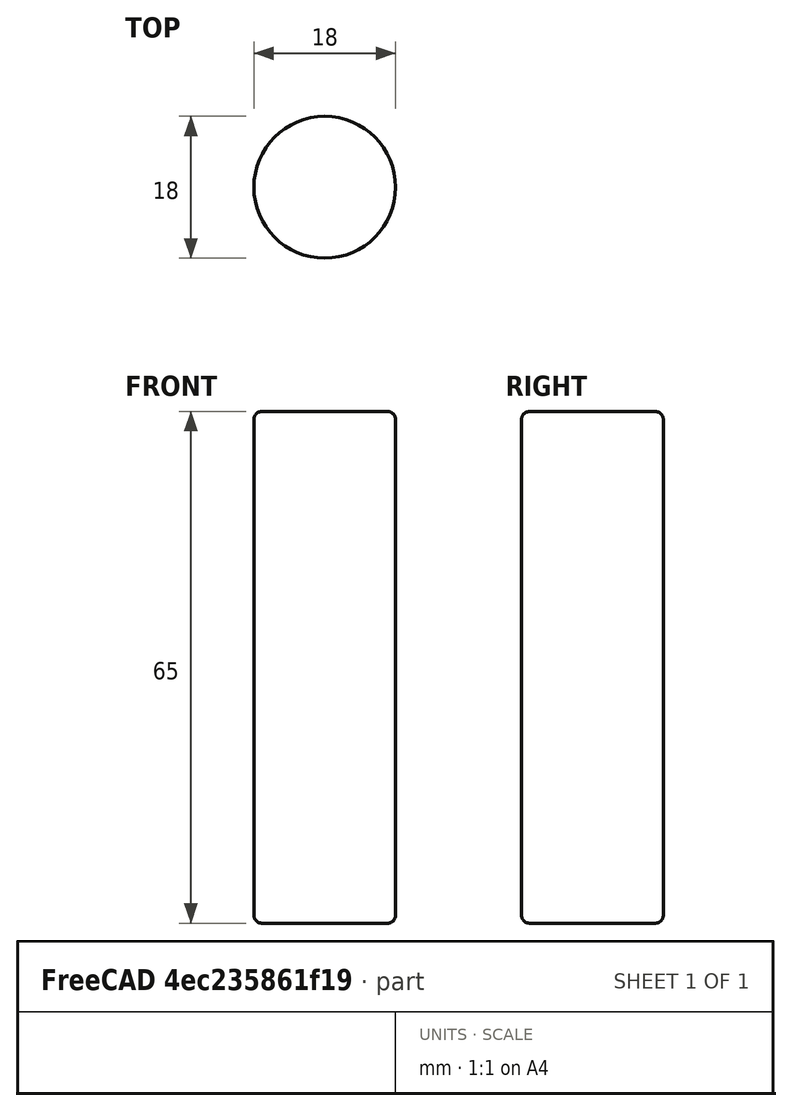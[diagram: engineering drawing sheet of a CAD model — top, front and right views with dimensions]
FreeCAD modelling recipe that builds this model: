
FCSTD DOCUMENT  (FreeCAD 0.20R29603 (Git))
Label: Battery
License: All rights reserved
LicenseURL: http://en.wikipedia.org/wiki/All_rights_reserved
objects: Sketcher::SketchObject×1, PartDesign::Pad×1, PartDesign::Fillet×1, PartDesign::Body×1
note: 6 computed .brp shape members not serialized (recipe doc carries the construction recipe); baked Part::Feature solids carry a one-line shape summary decoded from their .brp

FEATURE [Sketcher::SketchObject] Sketch
  FullyConstrained = true
  MapMode = 5
  Support = -> [XY_Plane]
  sketch-geometry (1):
    g0: Circle CenterX=0 CenterY=0 CenterZ=0 NormalX=0 NormalY=0 NormalZ=1 AngleXU=0 Radius=9
  constraints (2):
    c: Coincident(g0,g-1)
    c: Diameter(g0) = 18
FEATURE [PartDesign::Pad] Pad
  Direction = (0,0,1)
  Length = 65
  Length2 = 10
  Profile = -> Sketch
  ReferenceAxis = -> Sketch [N_Axis]
  Type = 0
FEATURE [PartDesign::Fillet] Fillet
  Base = -> Pad [Edge3,Edge2]
  BaseFeature = -> Pad
  Radius = 1
  SupportTransform = false
  UseAllEdges = false
FEATURE [PartDesign::Body] Body
  Group = -> [Sketch,Pad,Fillet]
  Origin = -> Origin
  Tip = -> Fillet
